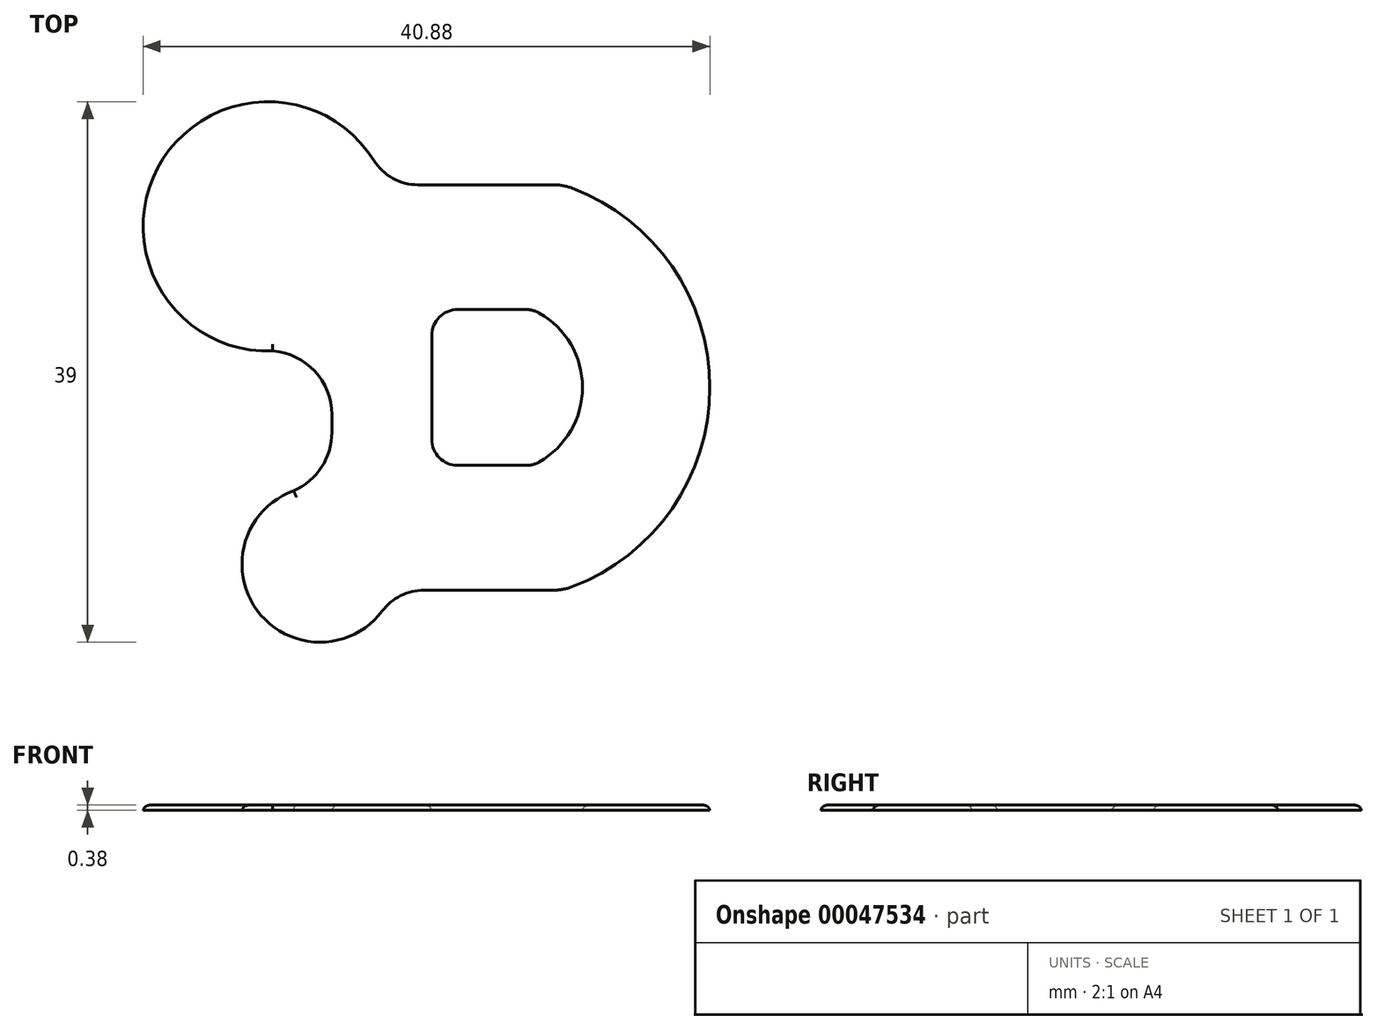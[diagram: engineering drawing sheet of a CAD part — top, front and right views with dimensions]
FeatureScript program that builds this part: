
annotation { "Feature Type Name" : "Feature", "Feature Type Description" : "" }
export const myFeature = defineFeature(function(context is Context, id is Id, definition is map)
    precondition{}
    {
        {
            var Q0;
            Q0=qCreatedBy(makeId("Top.planeOp"),FACE);
            var sketch = newSketch(context, id + "F0", { "sketchPlane" : qUnion([Q0])});
            skArc(sketch, "E0", {"start": v(20.36, 12.7) * mm, "mid": v(-21.2, 11.25) * mm, "end": v(0.9, -23.98) * mm});
            skArc(sketch, "E1", {"start": v(5.1, -50.82) * mm, "mid": v(-2.12, -73.84) * mm, "end": v(22, -74) * mm});
            skArc(sketch, "E2.trimOffspring", {"start": v(52.15, -45.35) * mm, "mid": v(60.5, -31) * mm, "end": v(52.15, -16.65) * mm});
            skArc(sketch, "E3.trimOffspring", {"start": v(58.49, -69.35) * mm, "mid": v(85, -31) * mm, "end": v(58.49, 7.35) * mm});
            skLineSegment(sketch, "E4", {"start": v(31.5, -21) * mm, "end": v(31.5, -41) * mm});
            skLineSegment(sketch, "E5", {"start": v(49.68, -16) * mm, "end": v(36.5, -16) * mm});
            skLineSegment(sketch, "E6", {"start": v(49.68, -46) * mm, "end": v(36.5, -46) * mm});
            skPoint(sketch, "E7.visualSharp", {"position": v(31.5, -16) * mm});
            skArc(sketch, "E7.filletArc", {"start": v(36.5, -16) * mm, "mid": v(32.96, -17.46) * mm, "end": v(31.5, -21) * mm});
            skPoint(sketch, "E8.visualSharp", {"position": v(31.5, -46) * mm});
            skArc(sketch, "E8.filletArc", {"start": v(31.5, -41) * mm, "mid": v(32.96, -44.54) * mm, "end": v(36.5, -46) * mm});
            skPoint(sketch, "E9.visualSharp", {"position": v(50.87, -16) * mm});
            skArc(sketch, "E9.filletArc", {"start": v(52.15, -16.65) * mm, "mid": v(50.96, -16.17) * mm, "end": v(49.68, -16) * mm});
            skPoint(sketch, "E10.visualSharp", {"position": v(50.87, -46) * mm});
            skArc(sketch, "E10.filletArc", {"start": v(49.68, -46) * mm, "mid": v(50.96, -45.83) * mm, "end": v(52.15, -45.35) * mm});
            skLineSegment(sketch, "E11", {"start": v(54.95, 8) * mm, "end": v(28.84, 8) * mm});
            skLineSegment(sketch, "E12", {"start": v(54.95, -70) * mm, "end": v(30, -70) * mm});
            skPoint(sketch, "E13.visualSharp", {"position": v(24.14, -70) * mm});
            skArc(sketch, "E13.filletArc", {"start": v(30, -70) * mm, "mid": v(25.53, -71.06) * mm, "end": v(22, -74) * mm});
            skPoint(sketch, "E14.visualSharp", {"position": v(22.63, 8) * mm});
            skArc(sketch, "E14.filletArc", {"start": v(20.36, 12.7) * mm, "mid": v(24, 9.26) * mm, "end": v(28.84, 8) * mm});
            skPoint(sketch, "E15.visualSharp", {"position": v(56.65, 8) * mm});
            skArc(sketch, "E15.filletArc", {"start": v(58.49, 7.35) * mm, "mid": v(56.75, 7.84) * mm, "end": v(54.95, 8) * mm});
            skPoint(sketch, "E16.visualSharp", {"position": v(56.65, -70) * mm});
            skArc(sketch, "E16.filletArc", {"start": v(54.95, -70) * mm, "mid": v(56.75, -69.84) * mm, "end": v(58.49, -69.35) * mm});
            skArc(sketch, "E17", {"start": v(12.3, -36.25) * mm, "mid": v(8.37, -27.24) * mm, "end": v(-0.9, -23.98) * mm});
            skPoint(sketch, "E18.visualSharp", {"position": v(7.11, -50.28) * mm});
            skArc(sketch, "E19", {"start": v(4.04, -51.23) * mm, "mid": v(10.02, -46.74) * mm, "end": v(12.3, -39.62) * mm});
            skLineSegment(sketch, "E20", {"start": v(12.3, -36.25) * mm, "end": v(12.3, -39.62) * mm});
            skSolve(sketch);
        }
        {
            var Q0;
            Q0 = qSketchRegion(id + "F0", true);
            extrude(context, id + "F1", {"entities" : qUnion([Q0]), "depth" : 1 * mm});
        }
        {
            var Q0;
            Q0=makeQuery(id+"F1.opExtrude","SWEPT_BODY",BODY,{"disambiguationData":[OSD([sQuery(id+"F0.wireOp",EDGE,"E0"),sQuery(id+"F0.wireOp",EDGE,"E1"),sQuery(id+"F0.wireOp",EDGE,"E2.trimOffspring"),sQuery(id+"F0.wireOp",EDGE,"E3.trimOffspring"),sQuery(id+"F0.wireOp",EDGE,"E4"),sQuery(id+"F0.wireOp",EDGE,"E5"),sQuery(id+"F0.wireOp",EDGE,"E6"),sQuery(id+"F0.wireOp",EDGE,"E7.filletArc"),sQuery(id+"F0.wireOp",EDGE,"E8.filletArc"),sQuery(id+"F0.wireOp",EDGE,"E9.filletArc"),sQuery(id+"F0.wireOp",EDGE,"E10.filletArc"),sQuery(id+"F0.wireOp",EDGE,"E11"),sQuery(id+"F0.wireOp",EDGE,"E12"),sQuery(id+"F0.wireOp",EDGE,"E13.filletArc"),sQuery(id+"F0.wireOp",EDGE,"E14.filletArc"),sQuery(id+"F0.wireOp",EDGE,"E15.filletArc"),sQuery(id+"F0.wireOp",EDGE,"E16.filletArc"),sQuery(id+"F0.wireOp",EDGE,"E17"),sQuery(id+"F0.wireOp",EDGE,"E19"),sQuery(id+"F0.wireOp",EDGE,"E20")])]});
            var Q1;
            Q1=qCreatedBy(makeId("Origin.pointOp"),VERTEX);
            transform(context, id + "F2", {"entities" : qUnion([Q0]), "transformType" : TransformType.SCALE_UNIFORMLY, "scale" : .5, "makeCopy" : false, "scalePoint" : qUnion([Q1])});
        }
        {
            var Q0;
            Q0=makeQuery(id+"F1.opExtrude","SWEPT_BODY",BODY,{"disambiguationData":[OSD([sQuery(id+"F0.wireOp",EDGE,"E0"),sQuery(id+"F0.wireOp",EDGE,"E1"),sQuery(id+"F0.wireOp",EDGE,"E2.trimOffspring"),sQuery(id+"F0.wireOp",EDGE,"E3.trimOffspring"),sQuery(id+"F0.wireOp",EDGE,"E4"),sQuery(id+"F0.wireOp",EDGE,"E5"),sQuery(id+"F0.wireOp",EDGE,"E6"),sQuery(id+"F0.wireOp",EDGE,"E7.filletArc"),sQuery(id+"F0.wireOp",EDGE,"E8.filletArc"),sQuery(id+"F0.wireOp",EDGE,"E9.filletArc"),sQuery(id+"F0.wireOp",EDGE,"E10.filletArc"),sQuery(id+"F0.wireOp",EDGE,"E11"),sQuery(id+"F0.wireOp",EDGE,"E12"),sQuery(id+"F0.wireOp",EDGE,"E13.filletArc"),sQuery(id+"F0.wireOp",EDGE,"E14.filletArc"),sQuery(id+"F0.wireOp",EDGE,"E15.filletArc"),sQuery(id+"F0.wireOp",EDGE,"E16.filletArc"),sQuery(id+"F0.wireOp",EDGE,"E17"),sQuery(id+"F0.wireOp",EDGE,"E19"),sQuery(id+"F0.wireOp",EDGE,"E20")])]});
            var Q1;
            Q1=qCreatedBy(makeId("Origin.pointOp"),VERTEX);
            transform(context, id + "F3", {"entities" : qUnion([Q0]), "transformType" : TransformType.SCALE_UNIFORMLY, "scale" : .75, "makeCopy" : false, "scalePoint" : qUnion([Q1])});
        }
        {
            var Q0;
            Q0=makeQuery(id+"F1.opExtrude","CAP_FACE",FACE,{"disambiguationData":[OSD([sQuery(id+"F0.wireOp",EDGE,"E0"),sQuery(id+"F0.wireOp",EDGE,"E1"),sQuery(id+"F0.wireOp",EDGE,"E2.trimOffspring"),sQuery(id+"F0.wireOp",EDGE,"E3.trimOffspring"),sQuery(id+"F0.wireOp",EDGE,"E4"),sQuery(id+"F0.wireOp",EDGE,"E5"),sQuery(id+"F0.wireOp",EDGE,"E6"),sQuery(id+"F0.wireOp",EDGE,"E7.filletArc"),sQuery(id+"F0.wireOp",EDGE,"E8.filletArc"),sQuery(id+"F0.wireOp",EDGE,"E9.filletArc"),sQuery(id+"F0.wireOp",EDGE,"E10.filletArc"),sQuery(id+"F0.wireOp",EDGE,"E11"),sQuery(id+"F0.wireOp",EDGE,"E12"),sQuery(id+"F0.wireOp",EDGE,"E13.filletArc"),sQuery(id+"F0.wireOp",EDGE,"E14.filletArc"),sQuery(id+"F0.wireOp",EDGE,"E15.filletArc"),sQuery(id+"F0.wireOp",EDGE,"E16.filletArc"),sQuery(id+"F0.wireOp",EDGE,"E17"),sQuery(id+"F0.wireOp",EDGE,"E19"),sQuery(id+"F0.wireOp",EDGE,"E20")])],"isStart":false});
            fillet(context, id + "F4", {"entities" : qUnion([Q0]), "radius" : .5 * mm, "tangentPropagation" : true, "allowEdgeOverflow" : false});
        }
    });
